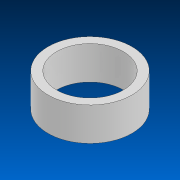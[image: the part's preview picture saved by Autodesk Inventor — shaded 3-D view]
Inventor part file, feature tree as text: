
AUTODESK INVENTOR PART (.ipt)
format: ipt  version: 2022 (Build 260153000, 153)  size: 86,528 bytes
history: native  units: in
note: dims shown in document units (in); Inventor stores cm internally (conversion verified against a paired STEP export)
features: extrude x1, sketch x1
ambient origin geometry x8: Origin, YZ Plane, XZ Plane, XY Plane, X Axis, Y Axis, Z Axis, Center Point
bodies: Solid1 (feature_tree)
feature tree (2):
  extrude  "Extrusion1"  Depth=0.436in
  sketch  "Sketch1"  dims[d0=0.875in d1=1.1in d2=0.436in d3=0.0in]
